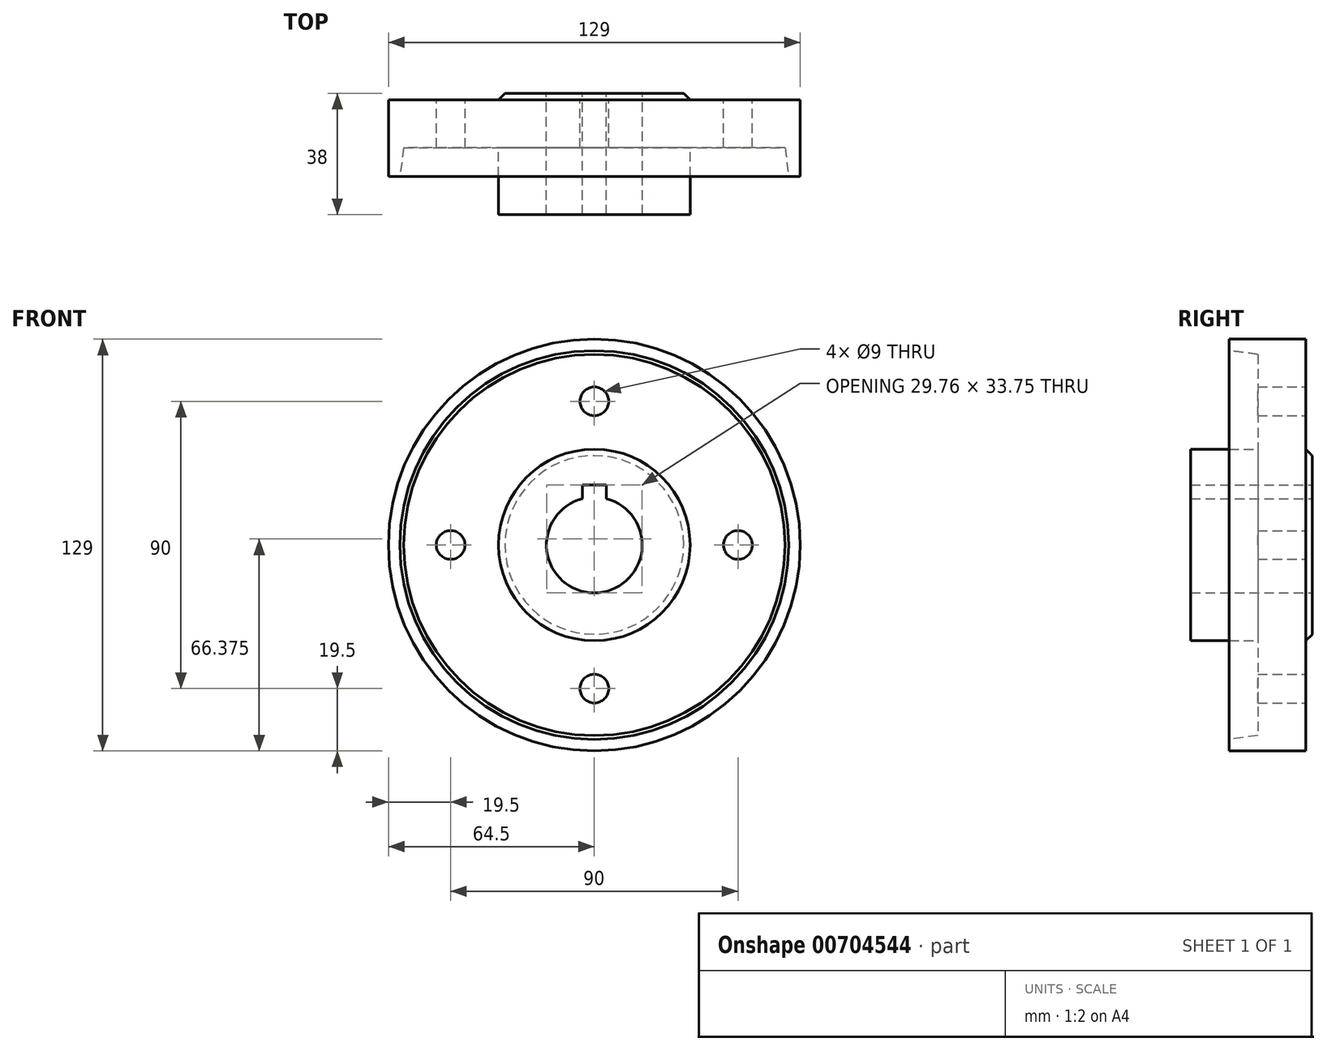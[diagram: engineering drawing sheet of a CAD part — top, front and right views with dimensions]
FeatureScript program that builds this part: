
annotation { "Feature Type Name" : "Feature", "Feature Type Description" : "" }
export const myFeature = defineFeature(function(context is Context, id is Id, definition is map)
    precondition{}
    {
        {
            var Q0;
            Q0=qCreatedBy(makeId("Right.planeOp"),FACE);
            var sketch = newSketch(context, id + "F0", { "sketchPlane" : qUnion([Q0])});
            skLineSegment(sketch, "E0", {"start": v(0, 64.5) * mm, "end": v(0, 0) * mm, "construction": true});
            skLineSegment(sketch, "E1", {"start": v(0, 64.5) * mm, "end": v(-24, 64.5) * mm});
            skLineSegment(sketch, "E2", {"start": v(-24, 64.5) * mm, "end": v(-24, 60.9) * mm});
            skLineSegment(sketch, "E3", {"start": v(-24, 60.9) * mm, "end": v(-15, 59.7) * mm});
            skLineSegment(sketch, "E4", {"start": v(-15, 59.7) * mm, "end": v(-15, 30) * mm});
            skLineSegment(sketch, "E5", {"start": v(-15, 30) * mm, "end": v(-36, 30) * mm});
            skLineSegment(sketch, "E6", {"start": v(-36, 30) * mm, "end": v(-36, 15) * mm});
            skLineSegment(sketch, "E7", {"start": v(-36, 15) * mm, "end": v(0, 15) * mm});
            skLineSegment(sketch, "E8", {"start": v(0, 64.5) * mm, "end": v(0, 15) * mm});
            skLineSegment(sketch, "E9", {"start": v(0, 0) * mm, "end": v(-56.53, 0) * mm, "construction": true});
            skSolve(sketch);
        }
        {
            var Q0;
            Q0 = qSketchRegion(id + "F0", true);
            var Q1;
            Q1=sQuery(id+"F0.wireOp",EDGE,"E9");
            revolve(context, id + "F1", {"surfaceOperationType" : NewSurfaceOperationType.NEW, "entities" : qUnion([Q0]), "axis" : qUnion([Q1]), "revolveType" : RevolveType.FULL});
        }
        {
            var Q0;
            Q0=makeQuery(id+"F1.opRevolve","SWEPT_FACE",FACE,{"disambiguationData":[OSD([sQuery(id+"F0.wireOp",EDGE,"E8")])]});
            var sketch = newSketch(context, id + "F2", { "sketchPlane" : qUnion([Q0])});
            skCircle(sketch, "E10", {"center": v(0, 0) * mm, "radius": 30 * mm});
            skCircle(sketch, "E11", {"center": v(0, 0) * mm, "radius": 15 * mm});
            skSolve(sketch);
        }
        {
            var Q0;
            Q0 = qSketchRegion(id + "F2", true);
            extrude(context, id + "F3", {"entities" : qUnion([Q0]), "operationType" : NewBodyOperationType.ADD, "depth" : 2 * mm, "offsetDistance" : 25 * mm});
        }
        {
            var Q0;
            Q0=makeQuery(id+"F3.opExtrude","CAP_EDGE",EDGE,{"disambiguationData":[OSD([sQuery(id+"F2.wireOp",EDGE,"E10")])],"isStart":false});
            chamfer(context, id + "F4", {"entities" : qUnion([Q0]), "width" : 2 * mm, "tangentPropagation" : true});
        }
        {
            var Q0;
            Q0=makeQuery(id+"F1.opRevolve","SWEPT_FACE",FACE,{"disambiguationData":[OSD([sQuery(id+"F0.wireOp",EDGE,"E8")])]});
            var sketch = newSketch(context, id + "F5", { "sketchPlane" : qUnion([Q0])});
            skCircle(sketch, "E12", {"center": v(0, 45) * mm, "radius": 4.5 * mm});
            skSolve(sketch);
        }
        {
            var Q0;
            Q0 = qSketchRegion(id + "F5", true);
            extrude(context, id + "F6", {"entities" : qUnion([Q0]), "operationType" : NewBodyOperationType.REMOVE, "oppositeDirection" : true, "depth" : 25 * mm, "offsetDistance" : 25 * mm});
        }
        {
            var Q0;
            Q0=makeQuery(id+"F6.boolean.opBoolean","COPY",FACE,{"derivedFrom":makeQuery(id+"F6.opExtrude","SWEPT_FACE",FACE,{"disambiguationData":[OSD([sQuery(id+"F5.wireOp",EDGE,"E12")])]})});
            var Q1;
            Q1=makeQuery(id+"F3.opExtrude","CAP_EDGE",EDGE,{"disambiguationData":[OSD([sQuery(id+"F2.wireOp",EDGE,"E11")])],"isStart":false});
            circularPattern(context, id + "F7", {"patternType" : PatternType.FACE, "faces" : qUnion([Q0]), "axis" : qUnion([Q1]), "angle" : 360 * degree, "instanceCount" : 4, "equalSpace" : true});
        }
        {
            var Q0;
            Q0=makeQuery(id+"F3.opExtrude","CAP_FACE",FACE,{"disambiguationData":[OSD([sQuery(id+"F2.wireOp",EDGE,"E10"),sQuery(id+"F2.wireOp",EDGE,"E11")])],"isStart":false});
            var sketch = newSketch(context, id + "F8", { "sketchPlane" : qUnion([Q0])});
            skLineSegment(sketch, "E13.bottom", {"start": v(3.75, 18.75) * mm, "end": v(-3.75, 18.75) * mm});
            skLineSegment(sketch, "E13.top", {"start": v(3.75, 11.25) * mm, "end": v(-3.75, 11.25) * mm});
            skLineSegment(sketch, "E13.left", {"start": v(3.75, 18.75) * mm, "end": v(3.75, 11.25) * mm});
            skLineSegment(sketch, "E13.right", {"start": v(-3.75, 18.75) * mm, "end": v(-3.75, 11.25) * mm});
            skPoint(sketch, "E13.middle", {"position": v(0, 15) * mm});
            skSolve(sketch);
        }
        {
            var Q0;
            Q0 = qSketchRegion(id + "F8", true);
            extrude(context, id + "F9", {"entities" : qUnion([Q0]), "operationType" : NewBodyOperationType.REMOVE, "oppositeDirection" : true, "depth" : 50 * mm, "offsetDistance" : 25 * mm});
        }
    });
